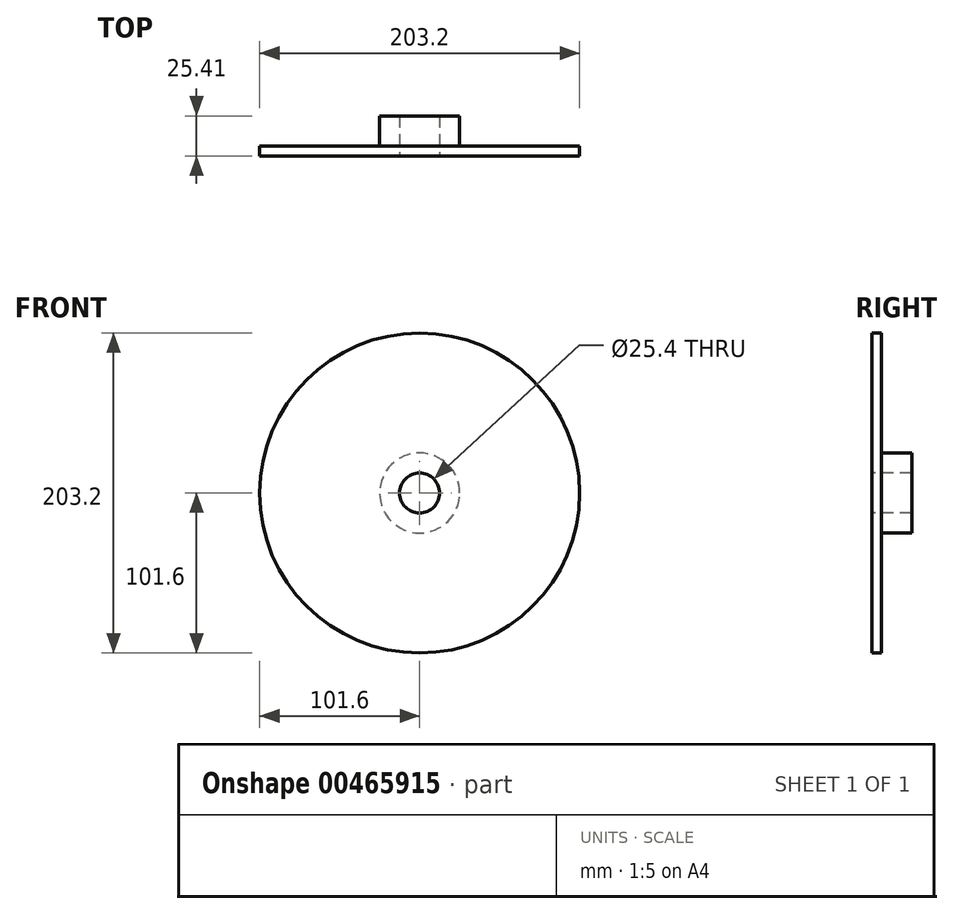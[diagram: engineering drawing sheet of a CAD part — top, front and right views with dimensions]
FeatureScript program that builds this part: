
annotation { "Feature Type Name" : "Feature", "Feature Type Description" : "" }
export const myFeature = defineFeature(function(context is Context, id is Id, definition is map)
    precondition{}
    {
        {
            var Q0;
            Q0=qCreatedBy(makeId("Front.planeOp"),FACE);
            var sketch = newSketch(context, id + "F0", { "sketchPlane" : qUnion([Q0])});
            skCircle(sketch, "E0", {"center": v(0, 0) * mm, "radius": 101.6 * mm});
            skSolve(sketch);
        }
        {
            var Q0;
            Q0=makeQuery(id+"F0.imprint","IMPRINT",FACE,{"disambiguationData":[TD([[makeQuery(id+"F0.imprint","IMPRINT",EDGE,{"derivedFrom":sQuery(id+"F0.wireOp",EDGE,"E0")}),1.0]])]});
            extrude(context, id + "F1", {"entities" : qUnion([Q0]), "endBound" : BoundingType.SYMMETRIC, "depth" : 6.35 * mm});
        }
        {
            var Q0;
            Q0=makeQuery(id+"F1.opExtrude","CAP_FACE",FACE,{"disambiguationData":[OSD([sQuery(id+"F0.wireOp",EDGE,"E0")])],"isStart":false});
            var sketch = newSketch(context, id + "F2", { "sketchPlane" : qUnion([Q0])});
            skCircle(sketch, "E1", {"center": v(0, 0) * mm, "radius": 25.4 * mm});
            skSolve(sketch);
        }
        {
            var Q0;
            Q0=makeQuery(id+"F2.imprint","IMPRINT",FACE,{"disambiguationData":[TD([[makeQuery(id+"F2.imprint","IMPRINT",EDGE,{"derivedFrom":sQuery(id+"F2.wireOp",EDGE,"E1")}),1.0]])]});
            extrude(context, id + "F3", {"entities" : qUnion([Q0]), "operationType" : NewBodyOperationType.ADD, "depth" : -25.4 * mm});
        }
        {
            var Q0;
            Q0=makeQuery(id+"F1.opExtrude","CAP_FACE",FACE,{"disambiguationData":[OSD([sQuery(id+"F0.wireOp",EDGE,"E0")])],"isStart":true});
            var sketch = newSketch(context, id + "F4", { "sketchPlane" : qUnion([Q0])});
            skCircle(sketch, "E2", {"center": v(0, 0) * mm, "radius": 12.7 * mm});
            skSolve(sketch);
        }
        {
            var Q0;
            Q0 = qSketchRegion(id + "F4", true);
            extrude(context, id + "F5", {"entities" : qUnion([Q0]), "operationType" : NewBodyOperationType.REMOVE, "endBound" : BoundingType.SYMMETRIC, "depth" : 127 * mm});
        }
    });
